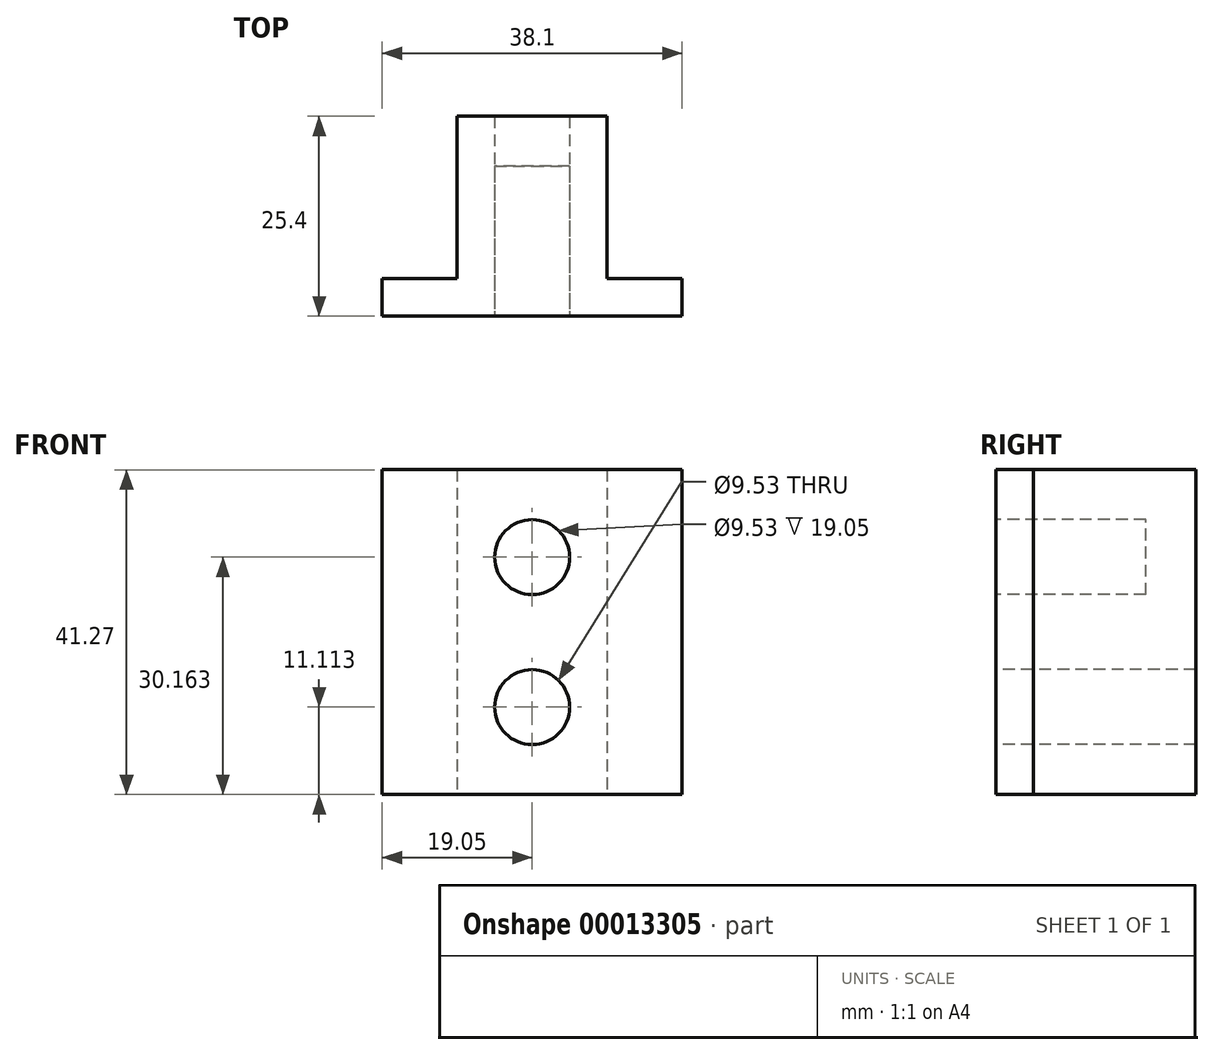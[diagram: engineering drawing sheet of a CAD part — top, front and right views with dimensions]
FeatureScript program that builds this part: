
annotation { "Feature Type Name" : "Feature", "Feature Type Description" : "" }
export const myFeature = defineFeature(function(context is Context, id is Id, definition is map)
    precondition{}
    {
        {
            var Q0;
            Q0=qCreatedBy(makeId("Top.planeOp"),FACE);
            var sketch = newSketch(context, id + "F0", { "sketchPlane" : qUnion([Q0])});
            skLineSegment(sketch, "E0", {"start": v(0, 0) * mm, "end": v(38.1, 0) * mm});
            skLineSegment(sketch, "E1", {"start": v(38.1, 0) * mm, "end": v(38.1, 4.76) * mm});
            skLineSegment(sketch, "E2", {"start": v(38.1, 4.76) * mm, "end": v(28.58, 4.76) * mm});
            skLineSegment(sketch, "E3", {"start": v(28.58, 4.76) * mm, "end": v(28.58, 25.4) * mm});
            skLineSegment(sketch, "E4", {"start": v(28.58, 25.4) * mm, "end": v(9.53, 25.4) * mm});
            skLineSegment(sketch, "E5", {"start": v(9.53, 25.4) * mm, "end": v(9.53, 4.76) * mm});
            skLineSegment(sketch, "E6", {"start": v(9.53, 4.76) * mm, "end": v(0, 4.76) * mm});
            skLineSegment(sketch, "E7", {"start": v(0, 4.76) * mm, "end": v(0, 0) * mm});
            skSolve(sketch);
        }
        {
            var Q0;
            Q0=makeQuery(id+"F0.imprint","IMPRINT",FACE,{"disambiguationData":[TD([[makeQuery(id+"F0.imprint","IMPRINT",EDGE,{"derivedFrom":sQuery(id+"F0.wireOp",EDGE,"E0")}),1.0]])]});
            extrude(context, id + "F1", {"entities" : qUnion([Q0]), "depth" : 41.27 * mm});
        }
        {
            var Q0;
            Q0=makeQuery(id+"F1.opExtrude","SWEPT_FACE",FACE,{"disambiguationData":[OSD([sQuery(id+"F0.wireOp",EDGE,"E0")])]});
            var sketch = newSketch(context, id + "F2", { "sketchPlane" : qUnion([Q0])});
            skCircle(sketch, "E8", {"center": v(19.05, 30.16) * mm, "radius": 4.76 * mm});
            skPoint(sketch, "E8.centerSnap0", {"position": v(19.05, 41.27) * mm});
            skCircle(sketch, "E9", {"center": v(19.05, 11.11) * mm, "radius": 4.76 * mm});
            skSolve(sketch);
        }
        {
            var Q0;
            Q0=makeQuery(id+"F2.imprint","IMPRINT",FACE,{"disambiguationData":[TD([[makeQuery(id+"F2.imprint","IMPRINT",EDGE,{"derivedFrom":sQuery(id+"F2.wireOp",EDGE,"E9")}),1.0]])]});
            extrude(context, id + "F3", {"entities" : qUnion([Q0]), "operationType" : NewBodyOperationType.REMOVE, "endBound" : BoundingType.THROUGH_ALL, "oppositeDirection" : true, "depth" : 25.4 * mm});
        }
        {
            var Q0;
            Q0=makeQuery(id+"F2.imprint","IMPRINT",FACE,{"disambiguationData":[TD([[makeQuery(id+"F2.imprint","IMPRINT",EDGE,{"derivedFrom":sQuery(id+"F2.wireOp",EDGE,"E8")}),1.0]])]});
            extrude(context, id + "F4", {"entities" : qUnion([Q0]), "operationType" : NewBodyOperationType.REMOVE, "oppositeDirection" : true, "depth" : 19.05 * mm});
        }
    });
